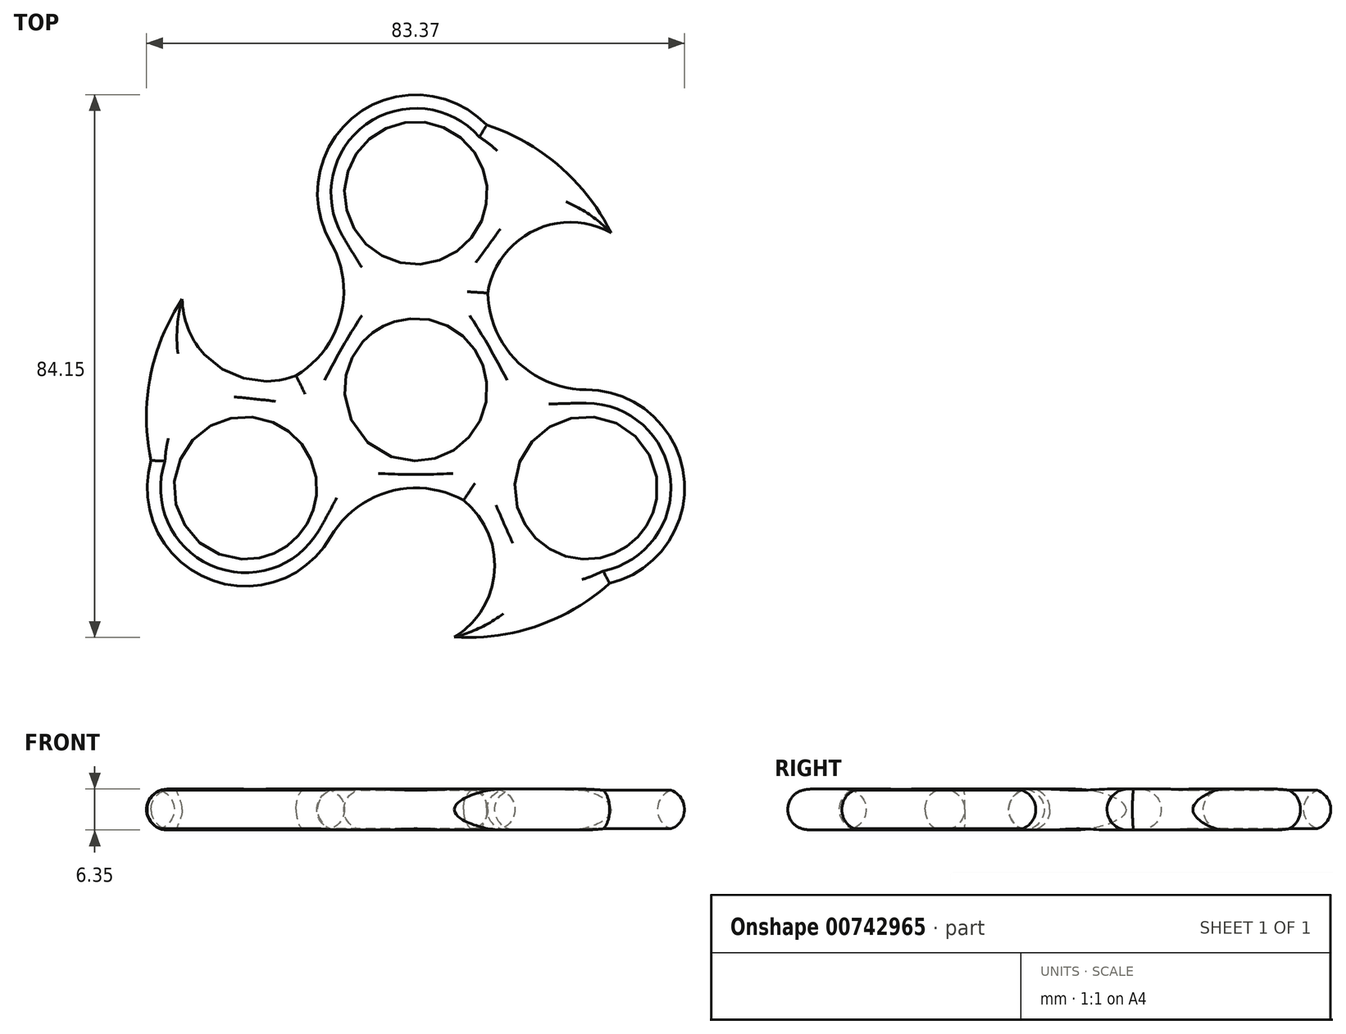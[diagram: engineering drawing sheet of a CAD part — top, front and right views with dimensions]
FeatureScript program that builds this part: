
annotation { "Feature Type Name" : "Feature", "Feature Type Description" : "" }
export const myFeature = defineFeature(function(context is Context, id is Id, definition is map)
    precondition{}
    {
        {
            var Q0;
            Q0=qCreatedBy(makeId("Top.planeOp"),FACE);
            var sketch = newSketch(context, id + "F0", { "sketchPlane" : qUnion([Q0])});
            skCircle(sketch, "E0", {"center": v(0, 0) * mm, "radius": 11.05 * mm});
            skCircle(sketch, "E1", {"center": v(0, 30.48) * mm, "radius": 11.05 * mm});
            skArc(sketch, "E2", {"start": v(11, 41.03) * mm, "mid": v(-9.15, 42.67) * mm, "end": v(-13.2, 22.86) * mm});
            skCircle(sketch, "E3.1.0", {"center": v(-26.4, -15.24) * mm, "radius": 11.05 * mm});
            skArc(sketch, "E3.1.1", {"start": v(-41.03, -10.99) * mm, "mid": v(-32.38, -29.26) * mm, "end": v(-13.2, -22.86) * mm});
            skCircle(sketch, "E3.2.0", {"center": v(26.4, -15.24) * mm, "radius": 11.05 * mm});
            skArc(sketch, "E3.2.1", {"start": v(30.03, -30.04) * mm, "mid": v(41.53, -13.41) * mm, "end": v(26.4, 0) * mm});
            skArc(sketch, "E4", {"start": v(-18.55, 2.17) * mm, "mid": v(-11.64, 11.42) * mm, "end": v(-13.2, 22.86) * mm});
            skArc(sketch, "E5.1.0", {"start": v(7.4, -17.15) * mm, "mid": v(-4.07, -15.8) * mm, "end": v(-13.2, -22.86) * mm});
            skArc(sketch, "E5.2.0", {"start": v(11.16, 14.98) * mm, "mid": v(15.71, 4.37) * mm, "end": v(26.4, 0) * mm});
            skArc(sketch, "E6", {"start": v(30.24, 24.34) * mm, "mid": v(22.3, 34.62) * mm, "end": v(11, 41.03) * mm});
            skArc(sketch, "E7", {"start": v(30.24, 24.34) * mm, "mid": v(18.26, 24.64) * mm, "end": v(11.16, 14.98) * mm});
            skArc(sketch, "E8.1.0", {"start": v(-36.2, 14.01) * mm, "mid": v(-41.14, 2) * mm, "end": v(-41.03, -10.99) * mm});
            skArc(sketch, "E8.1.1", {"start": v(-36.2, 14.01) * mm, "mid": v(-30.46, 3.5) * mm, "end": v(-18.55, 2.17) * mm});
            skArc(sketch, "E8.2.0", {"start": v(5.96, -38.36) * mm, "mid": v(18.84, -36.62) * mm, "end": v(30.03, -30.04) * mm});
            skArc(sketch, "E8.2.1", {"start": v(5.96, -38.36) * mm, "mid": v(12.2, -28.13) * mm, "end": v(7.4, -17.15) * mm});
            skPoint(sketch, "E9.orphan", {"position": v(13.2, 22.86) * mm});
            skPoint(sketch, "E10.orphan", {"position": v(13.2, -22.86) * mm});
            skPoint(sketch, "E11.orphan", {"position": v(-26.4, 0) * mm});
            skSolve(sketch);
        }
        {
            var Q0;
            Q0 = qSketchRegion(id + "F0", true);
            extrude(context, id + "F1", {"entities" : qUnion([Q0]), "depth" : 6.35 * mm, "offsetDistance" : 25.4 * mm});
        }
        {
            var Q0;
            Q0=makeQuery(id+"F1.opExtrude","CAP_FACE",FACE,{"disambiguationData":[OSD([sQuery(id+"F0.wireOp",EDGE,"ict1kz9F-ZJu5-n0xv-7yNY-cyaO9Ddmu6TZ"),sQuery(id+"F0.wireOp",EDGE,"E1"),sQuery(id+"F0.wireOp",EDGE,"E2"),sQuery(id+"F0.wireOp",EDGE,"E3.1.0"),sQuery(id+"F0.wireOp",EDGE,"E3.1.1"),sQuery(id+"F0.wireOp",EDGE,"E3.2.0"),sQuery(id+"F0.wireOp",EDGE,"E3.2.1"),sQuery(id+"F0.wireOp",EDGE,"E4"),sQuery(id+"F0.wireOp",EDGE,"E5.1.0"),sQuery(id+"F0.wireOp",EDGE,"E5.2.0")])],"isStart":false});
            var Q1;
            Q1=makeQuery(id+"F1.opExtrude","CAP_FACE",FACE,{"disambiguationData":[OSD([sQuery(id+"F0.wireOp",EDGE,"ict1kz9F-ZJu5-n0xv-7yNY-cyaO9Ddmu6TZ"),sQuery(id+"F0.wireOp",EDGE,"E1"),sQuery(id+"F0.wireOp",EDGE,"E2"),sQuery(id+"F0.wireOp",EDGE,"E3.1.0"),sQuery(id+"F0.wireOp",EDGE,"E3.1.1"),sQuery(id+"F0.wireOp",EDGE,"E3.2.0"),sQuery(id+"F0.wireOp",EDGE,"E3.2.1"),sQuery(id+"F0.wireOp",EDGE,"E4"),sQuery(id+"F0.wireOp",EDGE,"E5.1.0"),sQuery(id+"F0.wireOp",EDGE,"E5.2.0")])],"isStart":true});
            fillet(context, id + "F2", {"entities" : qUnion([Q0, Q1]), "radius" : 3.17 * mm, "tangentPropagation" : true, "allowEdgeOverflow" : false});
        }
    });
